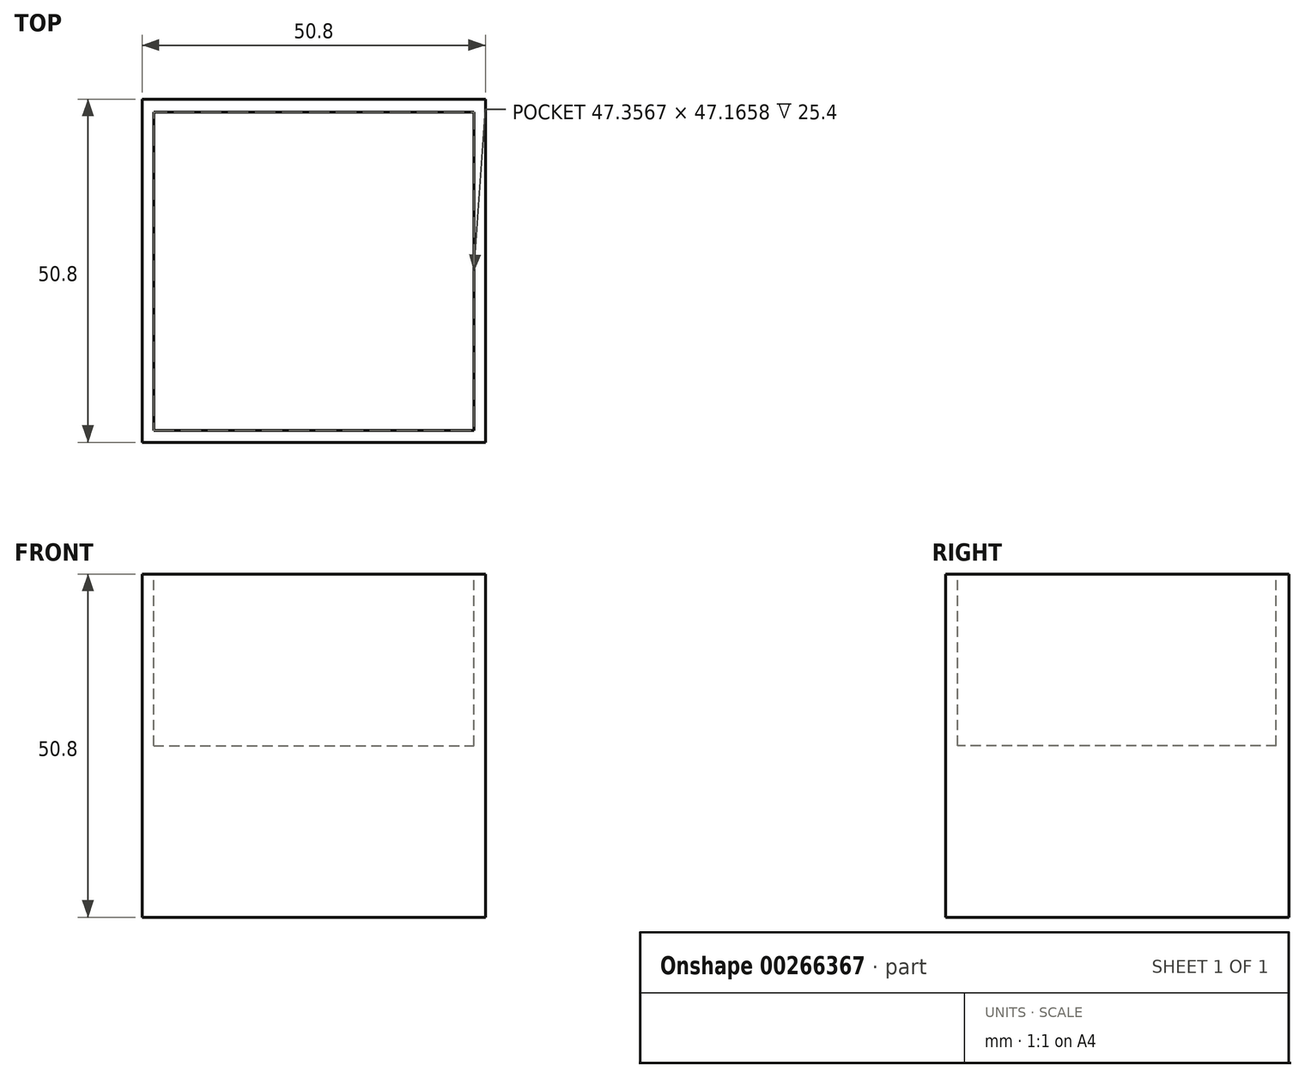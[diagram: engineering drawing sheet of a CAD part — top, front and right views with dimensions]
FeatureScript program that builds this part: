
annotation { "Feature Type Name" : "Feature", "Feature Type Description" : "" }
export const myFeature = defineFeature(function(context is Context, id is Id, definition is map)
    precondition{}
    {
        {
            var Q0;
            Q0=qCreatedBy(makeId("Front.planeOp"),FACE);
            var sketch = newSketch(context, id + "F0", { "sketchPlane" : qUnion([Q0])});
            skLineSegment(sketch, "E0.bottom", {"start": v(0, 0) * mm, "end": v(-50.8, 0) * mm});
            skLineSegment(sketch, "E0.top", {"start": v(0, 50.8) * mm, "end": v(-50.8, 50.8) * mm});
            skLineSegment(sketch, "E0.left", {"start": v(0, 0) * mm, "end": v(0, 50.8) * mm});
            skLineSegment(sketch, "E0.right", {"start": v(-50.8, 0) * mm, "end": v(-50.8, 50.8) * mm});
            skSolve(sketch);
        }
        {
            var Q0;
            Q0 = qSketchRegion(id + "F0", true);
            var Q1;
            Q1=makeQuery(id+"F0.imprint","IMPRINT",FACE,{"disambiguationData":[TD([[makeQuery(id+"F0.imprint","IMPRINT",EDGE,{"derivedFrom":sQuery(id+"F0.wireOp",EDGE,"E0.bottom")}),-1.0]])]});
            extrude(context, id + "F1", {"entities" : qUnion([Q0, Q1]), "depth" : 50.8 * mm});
        }
        {
            var Q0;
            Q0=makeQuery(id+"F1.opExtrude","SWEPT_FACE",FACE,{"disambiguationData":[OSD([sQuery(id+"F0.wireOp",EDGE,"E0.top")])]});
            var sketch = newSketch(context, id + "F2", { "sketchPlane" : qUnion([Q0])});
            skLineSegment(sketch, "E1.bottom", {"start": v(-49.08, -1.9) * mm, "end": v(-1.72, -1.9) * mm});
            skLineSegment(sketch, "E1.top", {"start": v(-49.08, -49.08) * mm, "end": v(-1.72, -49.08) * mm});
            skLineSegment(sketch, "E1.left", {"start": v(-49.08, -1.9) * mm, "end": v(-49.08, -49.08) * mm});
            skLineSegment(sketch, "E1.right", {"start": v(-1.72, -1.9) * mm, "end": v(-1.72, -49.08) * mm});
            skSolve(sketch);
        }
        {
            var Q0;
            Q0=makeQuery(id+"F2.imprint","IMPRINT",FACE,{"disambiguationData":[TD([[makeQuery(id+"F2.imprint","IMPRINT",EDGE,{"derivedFrom":sQuery(id+"F2.wireOp",EDGE,"E1.bottom")}),-1.0]])]});
            extrude(context, id + "F3", {"entities" : qUnion([Q0]), "operationType" : NewBodyOperationType.REMOVE, "oppositeDirection" : true, "depth" : 25.4 * mm});
        }
    });
